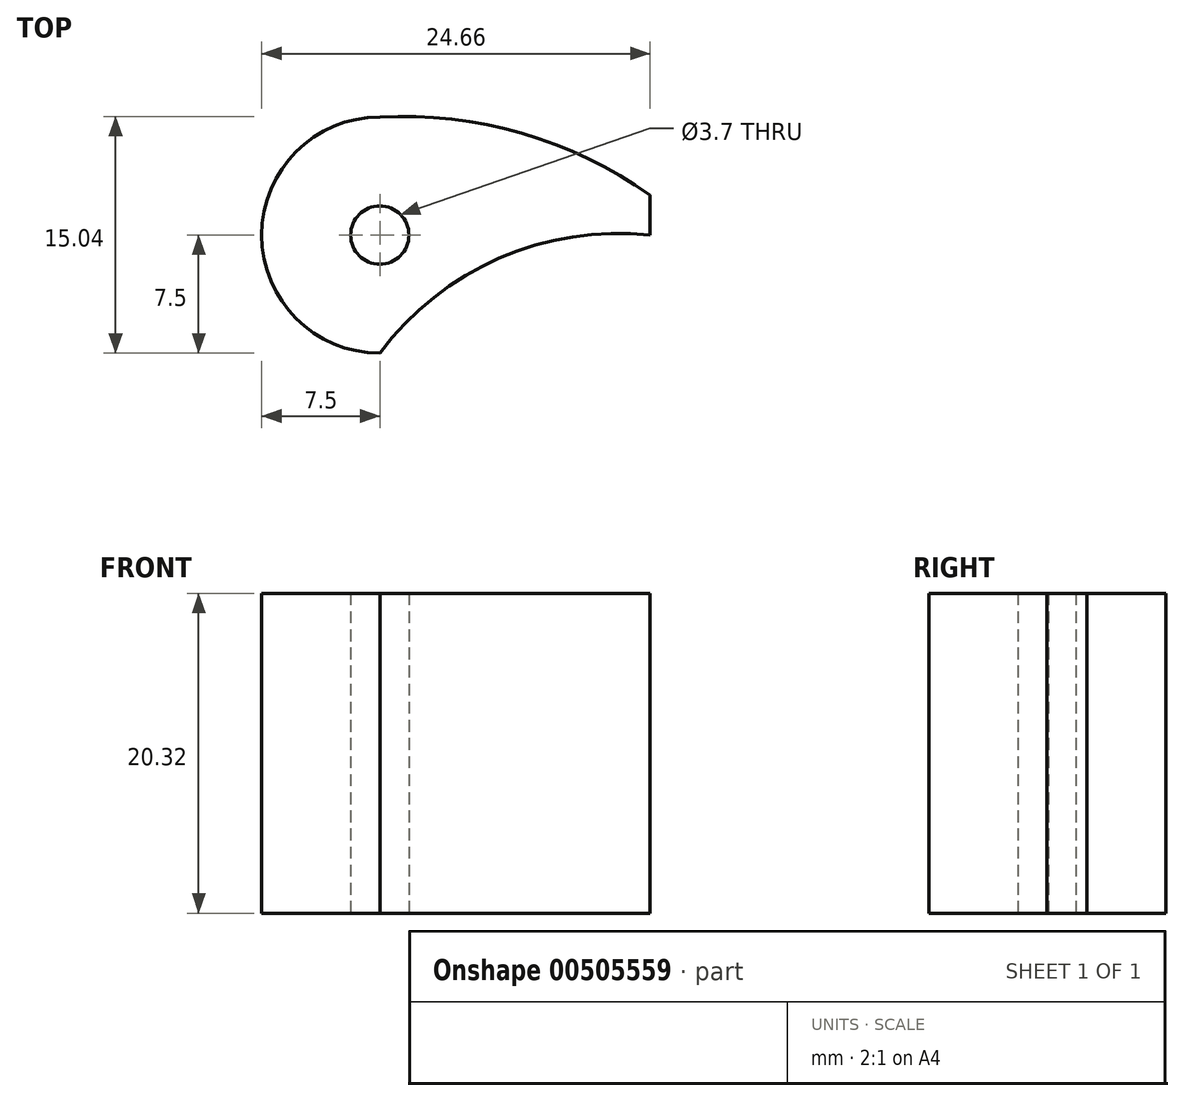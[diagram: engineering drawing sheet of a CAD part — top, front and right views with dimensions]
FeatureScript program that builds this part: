
annotation { "Feature Type Name" : "Feature", "Feature Type Description" : "" }
export const myFeature = defineFeature(function(context is Context, id is Id, definition is map)
    precondition{}
    {
        {
            var Q0;
            Q0=qCreatedBy(makeId("Top.planeOp"),FACE);
            var sketch = newSketch(context, id + "F0", { "sketchPlane" : qUnion([Q0])});
            skArc(sketch, "E0", {"start": v(7.33, -1.59) * mm, "mid": v(-4.7, 5.84) * mm, "end": v(0, -7.5) * mm});
            skCircle(sketch, "E1", {"center": v(0, 0) * mm, "radius": 1.85 * mm});
            skLineSegment(sketch, "E2", {"start": v(0, 0) * mm, "end": v(7.5, 0) * mm});
            skArc(sketch, "E3", {"start": v(17.16, 0) * mm, "mid": v(7.59, -1.47) * mm, "end": v(0, -7.5) * mm});
            skPoint(sketch, "E4.end.orphan", {"position": v(0, 7.5) * mm});
            skPoint(sketch, "E5", {"position": v(17.16, 2.54) * mm});
            skArc(sketch, "E6", {"start": v(17.16, 2.54) * mm, "mid": v(9, 6.48) * mm, "end": v(0, 7.5) * mm});
            skLineSegment(sketch, "E7", {"start": v(17.16, 2.54) * mm, "end": v(17.16, 0) * mm});
            skSolve(sketch);
        }
        {
            var Q0;
            Q0 = qSketchRegion(id + "F0", true);
            extrude(context, id + "F1", {"entities" : qUnion([Q0]), "depth" : 20.32 * mm});
        }
    });
